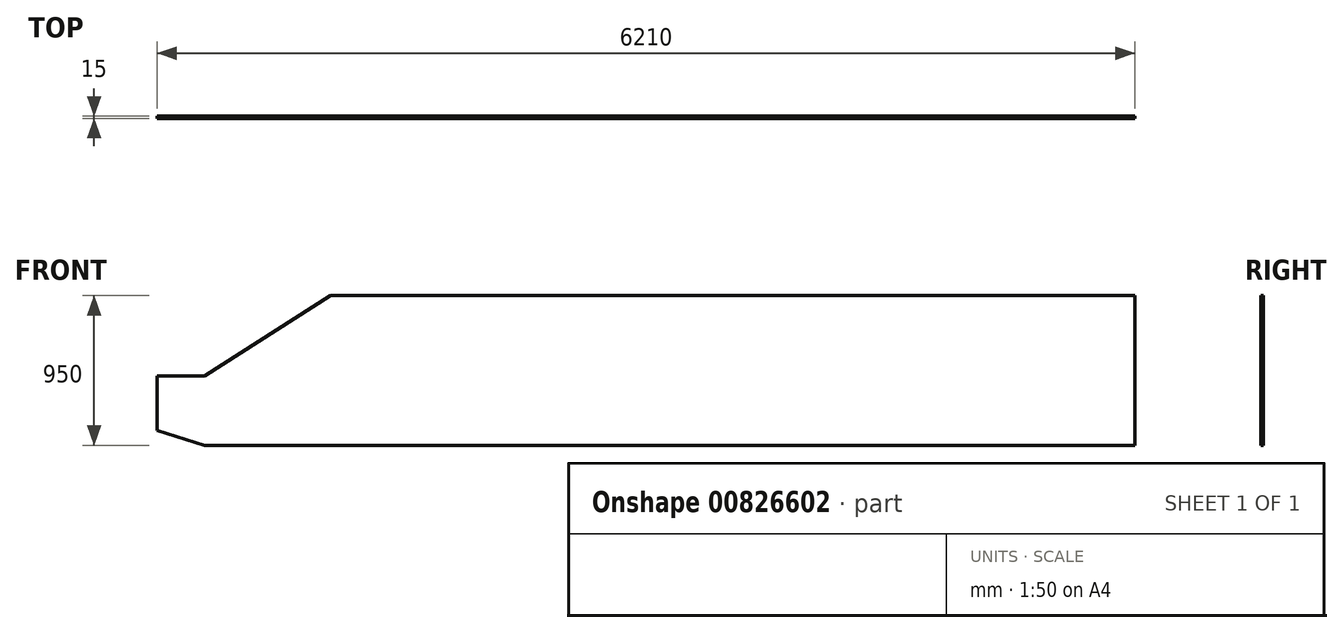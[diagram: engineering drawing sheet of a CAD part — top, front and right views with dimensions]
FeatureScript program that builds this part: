
annotation { "Feature Type Name" : "Feature", "Feature Type Description" : "" }
export const myFeature = defineFeature(function(context is Context, id is Id, definition is map)
    precondition{}
    {
        {
            var Q0;
            Q0=qCreatedBy(makeId("Front.planeOp"),FACE);
            var sketch = newSketch(context, id + "F0", { "sketchPlane" : qUnion([Q0])});
            skLineSegment(sketch, "E0", {"start": v(4325.49, 404.3) * mm, "end": v(4325.49, -545.7) * mm});
            skLineSegment(sketch, "E1", {"start": v(4325.49, -545.7) * mm, "end": v(-1584.51, -545.7) * mm});
            skLineSegment(sketch, "E2", {"start": v(-1584.51, -545.7) * mm, "end": v(-1884.51, -450.7) * mm});
            skLineSegment(sketch, "E3", {"start": v(-1884.51, -450.7) * mm, "end": v(-1884.51, -105.7) * mm});
            skLineSegment(sketch, "E4", {"start": v(-1884.51, -105.7) * mm, "end": v(-1584.51, -105.7) * mm});
            skLineSegment(sketch, "E5", {"start": v(-1584.51, -105.7) * mm, "end": v(-784.51, 404.3) * mm});
            skLineSegment(sketch, "E6", {"start": v(-784.51, 404.3) * mm, "end": v(4325.49, 404.3) * mm});
            skSolve(sketch);
        }
        {
            var Q0;
            Q0 = qSketchRegion(id + "F0", true);
            extrude(context, id + "F1", {"entities" : qUnion([Q0]), "depth" : 15 * mm, "offsetDistance" : 25 * mm});
        }
    });
